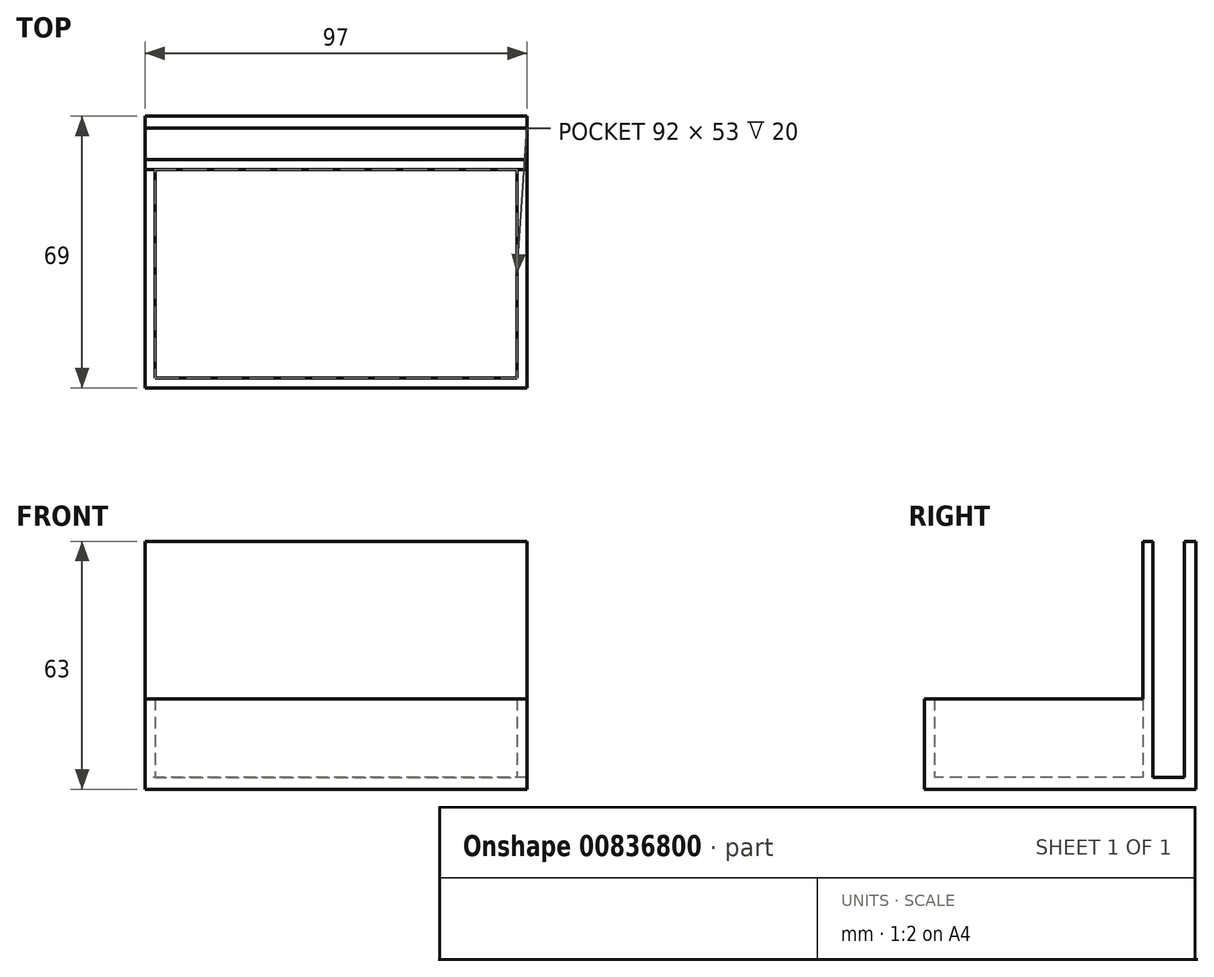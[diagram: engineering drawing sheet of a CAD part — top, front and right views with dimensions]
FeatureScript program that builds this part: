
annotation { "Feature Type Name" : "Feature", "Feature Type Description" : "" }
export const myFeature = defineFeature(function(context is Context, id is Id, definition is map)
    precondition{}
    {
        {
            var Q0;
            Q0=qCreatedBy(makeId("Top.planeOp"),FACE);
            var sketch = newSketch(context, id + "F0", { "sketchPlane" : qUnion([Q0])});
            skLineSegment(sketch, "E0.bottom", {"start": v(0, 0) * mm, "end": v(97, 0) * mm});
            skLineSegment(sketch, "E0.top", {"start": v(0, -58) * mm, "end": v(97, -58) * mm});
            skLineSegment(sketch, "E0.left", {"start": v(0, 0) * mm, "end": v(0, -58) * mm});
            skLineSegment(sketch, "E0.right", {"start": v(97, 0) * mm, "end": v(97, -58) * mm});
            skSolve(sketch);
        }
        {
            var Q0;
            Q0=makeQuery(id+"F0.imprint","IMPRINT",FACE,{"disambiguationData":[TD([[makeQuery(id+"F0.imprint","IMPRINT",EDGE,{"derivedFrom":sQuery(id+"F0.wireOp",EDGE,"E0.bottom")}),-1.0]])]});
            extrude(context, id + "F1", {"entities" : qUnion([Q0]), "depth" : 3 * mm, "offsetDistance" : 25 * mm});
        }
        {
            var Q0;
            Q0=makeQuery(id+"F1.opExtrude","CAP_FACE",FACE,{"disambiguationData":[OSD([sQuery(id+"F0.wireOp",EDGE,"E0.bottom"),sQuery(id+"F0.wireOp",EDGE,"E0.top"),sQuery(id+"F0.wireOp",EDGE,"E0.left"),sQuery(id+"F0.wireOp",EDGE,"E0.right")])],"isStart":false});
            var sketch = newSketch(context, id + "F2", { "sketchPlane" : qUnion([Q0])});
            skLineSegment(sketch, "E1.bottom", {"start": v(2.5, -2.5) * mm, "end": v(94.5, -2.5) * mm});
            skLineSegment(sketch, "E1.top", {"start": v(2.5, -55.5) * mm, "end": v(94.5, -55.5) * mm});
            skLineSegment(sketch, "E1.left", {"start": v(2.5, -2.5) * mm, "end": v(2.5, -55.5) * mm});
            skLineSegment(sketch, "E1.right", {"start": v(94.5, -2.5) * mm, "end": v(94.5, -55.5) * mm});
            skSolve(sketch);
        }
        {
            var Q0;
            Q0=makeQuery(id+"F2.imprint","IMPRINT",FACE,{"disambiguationData":[TD([[makeQuery(id+"F2.imprint","IMPRINT",EDGE,{"derivedFrom":sQuery(id+"F2.wireOp",EDGE,"E1.bottom")}),1.0]])]});
            extrude(context, id + "F3", {"entities" : qUnion([Q0]), "operationType" : NewBodyOperationType.ADD, "depth" : 20 * mm, "offsetDistance" : 25 * mm});
        }
        {
            var Q0;
            {var subQ0=sQuery(id+"F0.wireOp",EDGE,"E0.bottom");Q0=makeQuery(id+"F3.boolean.opBoolean","MERGE",FACE,{"derivedFrom":[makeQuery(id+"F1.opExtrude","SWEPT_FACE",FACE,{"disambiguationData":[OSD([subQ0])]}),makeQuery(id+"F3.opExtrude","SWEPT_FACE",FACE,{"disambiguationData":[OSD([subQ0])]})]});}
            var sketch = newSketch(context, id + "F4", { "sketchPlane" : qUnion([Q0])});
            skLineSegment(sketch, "E2.bottom", {"start": v(-97, 0) * mm, "end": v(0, 0) * mm});
            skLineSegment(sketch, "E2.top", {"start": v(-97, 3) * mm, "end": v(0, 3) * mm});
            skLineSegment(sketch, "E2.left", {"start": v(-97, 0) * mm, "end": v(-97, 3) * mm});
            skLineSegment(sketch, "E2.right", {"start": v(0, 0) * mm, "end": v(0, 3) * mm});
            skSolve(sketch);
        }
        {
            var Q0;
            Q0=makeQuery(id+"F4.imprint","IMPRINT",FACE,{"disambiguationData":[TD([[makeQuery(id+"F4.imprint","IMPRINT",EDGE,{"derivedFrom":sQuery(id+"F4.wireOp",EDGE,"E2.bottom")}),-1.0]])]});
            extrude(context, id + "F5", {"entities" : qUnion([Q0]), "operationType" : NewBodyOperationType.ADD, "depth" : 11 * mm, "offsetDistance" : 25 * mm});
        }
        {
            var Q0;
            Q0=makeQuery(id+"F3.opExtrude","CAP_FACE",FACE,{"disambiguationData":[OSD([sQuery(id+"F0.wireOp",EDGE,"E0.bottom"),sQuery(id+"F0.wireOp",EDGE,"E0.top"),sQuery(id+"F0.wireOp",EDGE,"E0.left"),sQuery(id+"F0.wireOp",EDGE,"E0.right"),sQuery(id+"F2.wireOp",EDGE,"E1.bottom"),sQuery(id+"F2.wireOp",EDGE,"E1.top"),sQuery(id+"F2.wireOp",EDGE,"E1.left"),sQuery(id+"F2.wireOp",EDGE,"E1.right")])],"isStart":false});
            var sketch = newSketch(context, id + "F6", { "sketchPlane" : qUnion([Q0])});
            skLineSegment(sketch, "E3.bottom", {"start": v(97, 0) * mm, "end": v(0, 0) * mm});
            skLineSegment(sketch, "E3.top", {"start": v(97, -2.5) * mm, "end": v(0, -2.5) * mm});
            skLineSegment(sketch, "E3.left", {"start": v(97, 0) * mm, "end": v(97, -2.5) * mm});
            skLineSegment(sketch, "E3.right", {"start": v(0, 0) * mm, "end": v(0, -2.5) * mm});
            skSolve(sketch);
        }
        {
            var Q0;
            Q0=makeQuery(id+"F6.imprint","IMPRINT",FACE,{"disambiguationData":[TD([[makeQuery(id+"F6.imprint","IMPRINT",EDGE,{"derivedFrom":sQuery(id+"F6.wireOp",EDGE,"E3.bottom")}),-1.0]])]});
            extrude(context, id + "F7", {"entities" : qUnion([Q0]), "operationType" : NewBodyOperationType.ADD, "depth" : 40 * mm, "offsetDistance" : 25 * mm});
        }
        {
            var Q0;
            Q0=makeQuery(id+"F5.opExtrude","SWEPT_FACE",FACE,{"disambiguationData":[OSD([sQuery(id+"F4.wireOp",EDGE,"E2.top")])]});
            var sketch = newSketch(context, id + "F8", { "sketchPlane" : qUnion([Q0])});
            skLineSegment(sketch, "E4.bottom", {"start": v(0, 11) * mm, "end": v(97, 11) * mm});
            skLineSegment(sketch, "E4.top", {"start": v(0, 8) * mm, "end": v(97, 8) * mm});
            skLineSegment(sketch, "E4.left", {"start": v(0, 11) * mm, "end": v(0, 8) * mm});
            skLineSegment(sketch, "E4.right", {"start": v(97, 11) * mm, "end": v(97, 8) * mm});
            skSolve(sketch);
        }
        {
            var Q0;
            Q0=makeQuery(id+"F8.imprint","IMPRINT",FACE,{"disambiguationData":[TD([[makeQuery(id+"F8.imprint","IMPRINT",EDGE,{"derivedFrom":sQuery(id+"F8.wireOp",EDGE,"E4.bottom")}),1.0]])]});
            var Q1;
            Q1=makeQuery(id+"F7.opExtrude","CAP_FACE",FACE,{"disambiguationData":[OSD([sQuery(id+"F6.wireOp",EDGE,"E3.bottom"),sQuery(id+"F6.wireOp",EDGE,"E3.top"),sQuery(id+"F6.wireOp",EDGE,"E3.left"),sQuery(id+"F6.wireOp",EDGE,"E3.right")])],"isStart":false});
            extrude(context, id + "F9", {"entities" : qUnion([Q0]), "operationType" : NewBodyOperationType.ADD, "endBound" : BoundingType.UP_TO_SURFACE, "depth" : 25 * mm, "endBoundEntityFace" : qUnion([Q1]), "offsetDistance" : 25 * mm});
        }
    });
